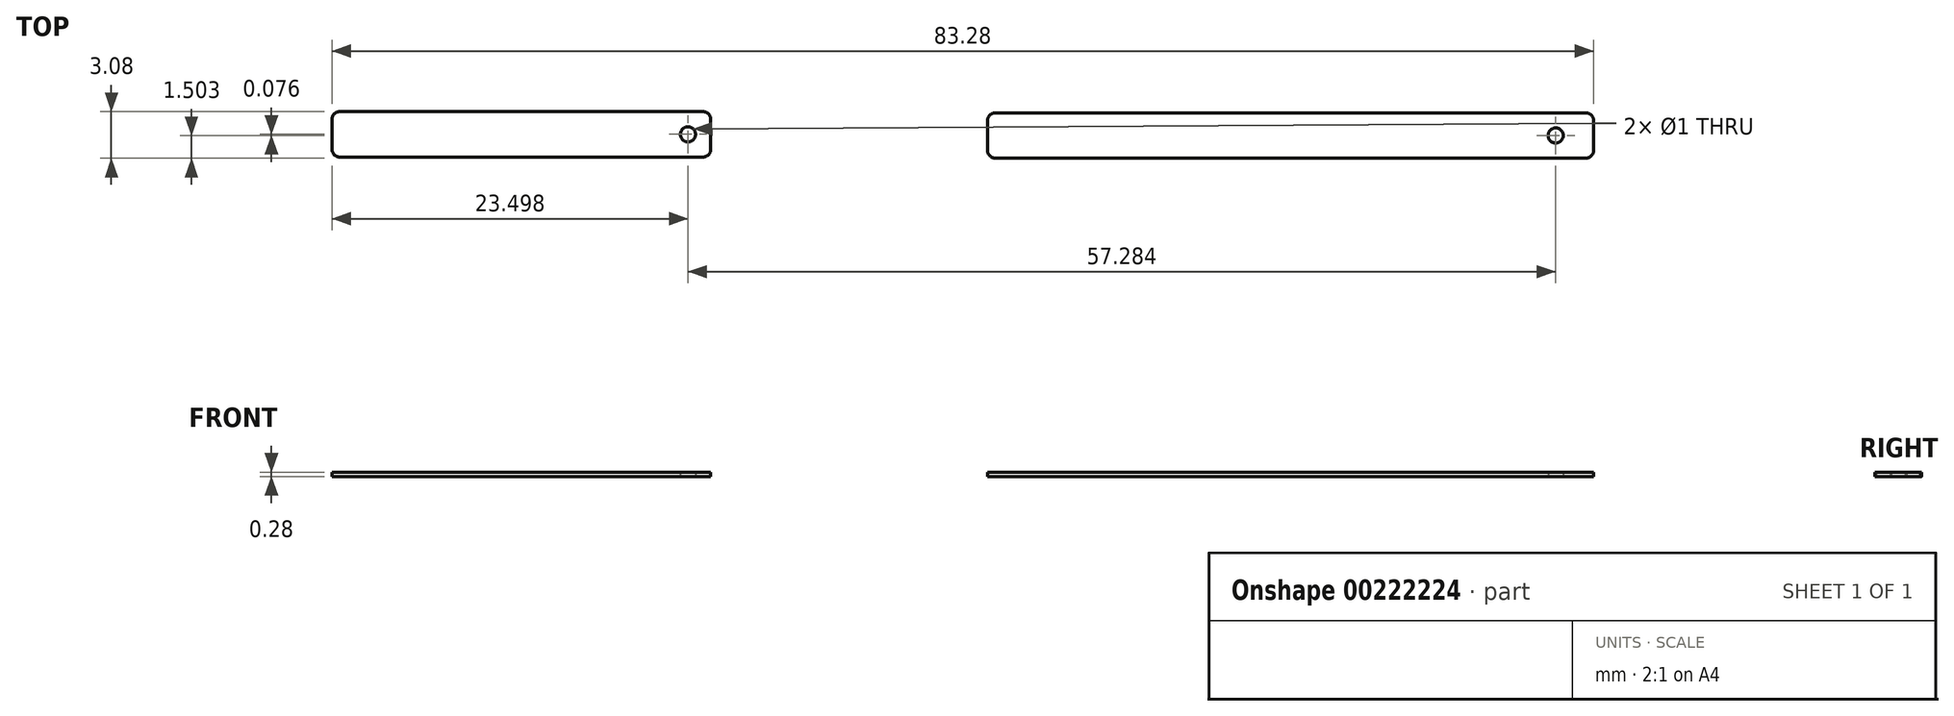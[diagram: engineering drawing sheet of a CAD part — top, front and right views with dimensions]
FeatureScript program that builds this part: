
annotation { "Feature Type Name" : "Feature", "Feature Type Description" : "" }
export const myFeature = defineFeature(function(context is Context, id is Id, definition is map)
    precondition{}
    {
        {
            var Q0;
            Q0=qCreatedBy(makeId("Top.planeOp"),FACE);
            var sketch = newSketch(context, id + "F0", { "sketchPlane" : qUnion([Q0])});
            skLineSegment(sketch, "E0.bottom", {"start": v(2.88, 12.64) * mm, "end": v(41.88, 12.64) * mm});
            skLineSegment(sketch, "E0.top", {"start": v(2.88, 15.64) * mm, "end": v(41.88, 15.64) * mm});
            skLineSegment(sketch, "E0.left", {"start": v(2.38, 15.14) * mm, "end": v(2.38, 13.14) * mm});
            skLineSegment(sketch, "E0.right", {"start": v(42.38, 15.14) * mm, "end": v(42.38, 13.14) * mm});
            skCircle(sketch, "E1", {"center": v(39.88, 14.14) * mm, "radius": 0.5 * mm});
            skPoint(sketch, "E2.visualSharp", {"position": v(2.38, 15.64) * mm});
            skArc(sketch, "E2.filletArc", {"start": v(2.88, 15.64) * mm, "mid": v(2.53, 15.5) * mm, "end": v(2.38, 15.14) * mm});
            skPoint(sketch, "E3.visualSharp", {"position": v(2.38, 12.64) * mm});
            skArc(sketch, "E3.filletArc", {"start": v(2.38, 13.14) * mm, "mid": v(2.53, 12.79) * mm, "end": v(2.88, 12.64) * mm});
            skPoint(sketch, "E4.visualSharp", {"position": v(42.38, 15.64) * mm});
            skArc(sketch, "E4.filletArc", {"start": v(42.38, 15.14) * mm, "mid": v(42.24, 15.5) * mm, "end": v(41.88, 15.64) * mm});
            skPoint(sketch, "E5.visualSharp", {"position": v(42.38, 12.64) * mm});
            skArc(sketch, "E5.filletArc", {"start": v(41.88, 12.64) * mm, "mid": v(42.24, 12.79) * mm, "end": v(42.38, 13.14) * mm});
            skSolve(sketch);
        }
        {
            var Q0;
            Q0=makeQuery(id+"F0.imprint","IMPRINT",FACE,{"disambiguationData":[TD([[makeQuery(id+"F0.imprint","IMPRINT",EDGE,{"derivedFrom":sQuery(id+"F0.wireOp",EDGE,"E0.bottom")}),1.0]])]});
            extrude(context, id + "F1", {"entities" : qUnion([Q0]), "depth" : 0.28 * mm});
        }
        {
            var Q0;
            Q0=qCreatedBy(makeId("Top.planeOp"),FACE);
            var sketch = newSketch(context, id + "F2", { "sketchPlane" : qUnion([Q0])});
            skLineSegment(sketch, "E6.bottom", {"start": v(-40.4, 12.72) * mm, "end": v(-16.4, 12.72) * mm});
            skLineSegment(sketch, "E6.top", {"start": v(-40.4, 15.72) * mm, "end": v(-16.4, 15.72) * mm});
            skLineSegment(sketch, "E6.left", {"start": v(-40.9, 15.22) * mm, "end": v(-40.9, 13.22) * mm});
            skLineSegment(sketch, "E6.right", {"start": v(-15.9, 15.22) * mm, "end": v(-15.9, 13.22) * mm});
            skCircle(sketch, "E7", {"center": v(-17.4, 14.22) * mm, "radius": 0.5 * mm});
            skPoint(sketch, "E8.visualSharp", {"position": v(-40.9, 15.72) * mm});
            skArc(sketch, "E8.filletArc", {"start": v(-40.4, 15.72) * mm, "mid": v(-40.76, 15.57) * mm, "end": v(-40.9, 15.22) * mm});
            skPoint(sketch, "E9.visualSharp", {"position": v(-40.9, 12.72) * mm});
            skArc(sketch, "E9.filletArc", {"start": v(-40.9, 13.22) * mm, "mid": v(-40.76, 12.87) * mm, "end": v(-40.4, 12.72) * mm});
            skPoint(sketch, "E10.visualSharp", {"position": v(-15.9, 15.72) * mm});
            skArc(sketch, "E10.filletArc", {"start": v(-15.9, 15.22) * mm, "mid": v(-16.05, 15.57) * mm, "end": v(-16.4, 15.72) * mm});
            skPoint(sketch, "E11.visualSharp", {"position": v(-15.9, 12.72) * mm});
            skArc(sketch, "E11.filletArc", {"start": v(-16.4, 12.72) * mm, "mid": v(-16.05, 12.87) * mm, "end": v(-15.9, 13.22) * mm});
            skSolve(sketch);
        }
        {
            var Q0;
            Q0=makeQuery(id+"F2.imprint","IMPRINT",FACE,{"disambiguationData":[TD([[makeQuery(id+"F2.imprint","IMPRINT",EDGE,{"derivedFrom":sQuery(id+"F2.wireOp",EDGE,"E6.bottom")}),1.0]])]});
            extrude(context, id + "F3", {"entities" : qUnion([Q0]), "depth" : 0.28 * mm});
        }
    });
